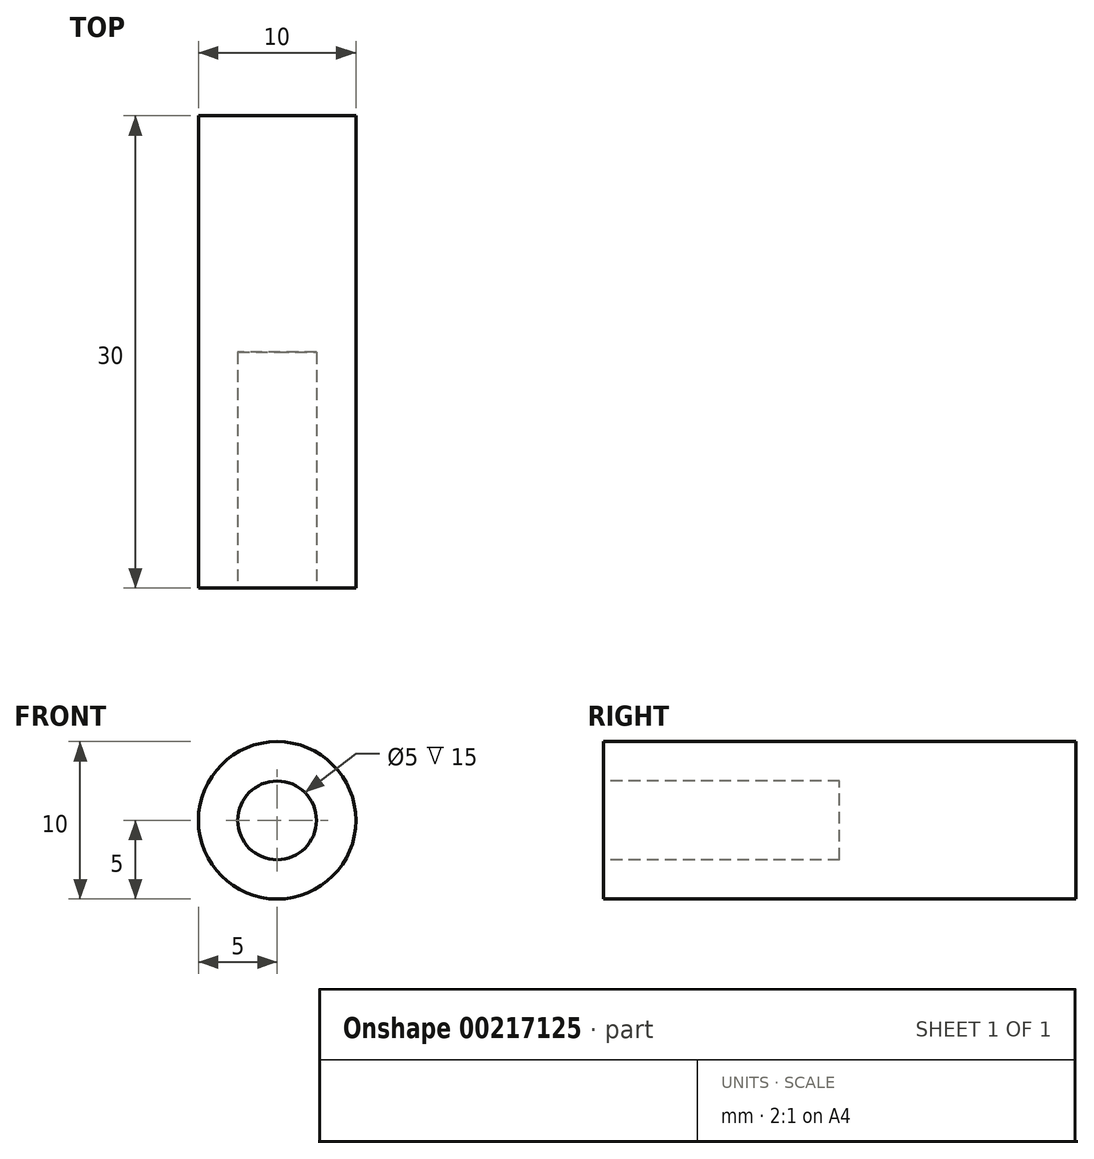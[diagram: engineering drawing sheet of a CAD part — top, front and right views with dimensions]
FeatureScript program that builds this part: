
annotation { "Feature Type Name" : "Feature", "Feature Type Description" : "" }
export const myFeature = defineFeature(function(context is Context, id is Id, definition is map)
    precondition{}
    {
        {
            var Q0;
            Q0=qCreatedBy(makeId("Front.planeOp"),FACE);
            var sketch = newSketch(context, id + "F0", { "sketchPlane" : qUnion([Q0])});
            skCircle(sketch, "E0", {"center": v(0, 0) * mm, "radius": 5 * mm});
            skCircle(sketch, "E1", {"center": v(0, 0) * mm, "radius": 2.5 * mm});
            skSolve(sketch);
        }
        {
            var Q0;
            Q0=makeQuery(id+"F0.imprint","IMPRINT",FACE,{"disambiguationData":[TD([[makeQuery(id+"F0.imprint","IMPRINT",EDGE,{"derivedFrom":sQuery(id+"F0.wireOp",EDGE,"E0")}),1.0]])]});
            var Q1;
            Q1=makeQuery(id+"F0.imprint","IMPRINT",FACE,{"disambiguationData":[TD([[makeQuery(id+"F0.imprint","IMPRINT",EDGE,{"derivedFrom":sQuery(id+"F0.wireOp",EDGE,"E1")}),1.0]])]});
            extrude(context, id + "F1", {"entities" : qUnion([Q0, Q1]), "depth" : 30 * mm});
        }
        {
            var Q0;
            Q0=makeQuery(id+"F1.opExtrude","CAP_FACE",FACE,{"disambiguationData":[OSD([sQuery(id+"F0.wireOp",EDGE,"E0")])],"isStart":false});
            var sketch = newSketch(context, id + "F2", { "sketchPlane" : qUnion([Q0])});
            skCircle(sketch, "E2", {"center": v(0, 0) * mm, "radius": 2.5 * mm});
            skSolve(sketch);
        }
        {
            var Q0;
            Q0=makeQuery(id+"F2.imprint","IMPRINT",FACE,{"disambiguationData":[TD([[makeQuery(id+"F2.imprint","IMPRINT",EDGE,{"derivedFrom":sQuery(id+"F2.wireOp",EDGE,"E2")}),1.0]])]});
            extrude(context, id + "F3", {"entities" : qUnion([Q0]), "operationType" : NewBodyOperationType.REMOVE, "oppositeDirection" : true, "depth" : 15 * mm});
        }
    });
